# Revit family: CADS_Vent-Axia_Lo-CarbonSentinelKineticHighFlow
name_source: partatom
category: Mechanical Equipment
revit_build: Autodesk Revit 2015 (Build: 20160512_1515(x64)
units: mm (PartAtom-declared; Revit-internal decimal feet)

## types (2) — shared parameters
Apparent Load = 690 VA
AssetType = Fixed
Category = Pr_60_60_36:Heat recovery distribution equipment
Color = White
DurationUnit = year
ExpectedLife = 20
Features = Humidistat
IfcExportAs = IfcAirToAirHeatRecoveryType
IfcExportType = USERDEFINED
Manufacturer = Vent-Axia Limited
Material = ABS Plastic
Name = MVHR Unit
NominalHeight = 635 mm  [stored 2.08333 ft]
NominalLength = 785 mm
NominalWidth = 550 mm
NumberOfPoles = 1
RatedCurrent = 3 A
RatedVoltage = 230 V
Shape = Rectangular
Size = 550mm x 785mm x 635mm 
285mm x 550mm x 550mm
SpigotConnLength = 250 mm  [stored 0.82021 ft]
SpigotConnWidth = 210 mm  [stored 0.688976 ft]
SpigotCrsLength = 520 mm  [stored 1.70604 ft]
SpigotCrsWidth = 275 mm
SpigotHeight = 87 mm  [stored 0.285433 ft]
SpigotOffset = 133 mm
Version = 1.0
WarrantyDurationLabor = 2
WarrantyDurationMotors = 5
WarrantyDurationParts = 2
WarrantyDurationUnit = year

## per-type parameters (varying)
| type | Description | LeftHand | Model | ModelNumber | ModelReference | RightHand |
| Right Hand | Lo-Carbon Sentinel Kinetic High Flow Right | No | Kinetic High Flow Right | 408449 | Kinetic High Flow Right | Yes |
| Left Hand | Lo-Carbon Sentinel Kinetic High Flow Left | Yes | Kinetic High Flow Left | 408451
408451
408451 | Kinetic High Flow Left | No |

note: [stored X ft] marks values corroborated as IEEE doubles in the binary element streams (Revit-internal decimal feet)

## geometry (parser evidence)
native form markers: Sweep x26
no freeform markers — native parametric forms only
